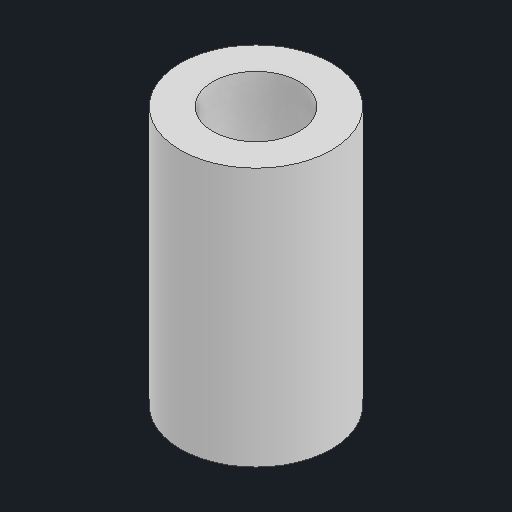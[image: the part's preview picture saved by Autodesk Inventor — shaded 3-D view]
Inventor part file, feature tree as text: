
AUTODESK INVENTOR PART (.ipt)
format: ipt  version: 2024 (Build 280153000, 153)  size: 87,552 bytes
history: native  units: in
note: dims shown in document units (in); Inventor stores cm internally (conversion verified against a paired STEP export)
features: other x3, sketch x1
ambient origin geometry x8: Origin, YZ Plane, XZ Plane, XY Plane, X Axis, Y Axis, Z Axis, Center Point
bodies: Solid1 (feature_tree)
feature tree (4):
  other  "12mm spacer.ipt"
  other  "Solid1::12mm spacer.ipt"
  other  "TaggingFeature1"
  sketch  "Sketch1"  dims[d0=0.3937in]
